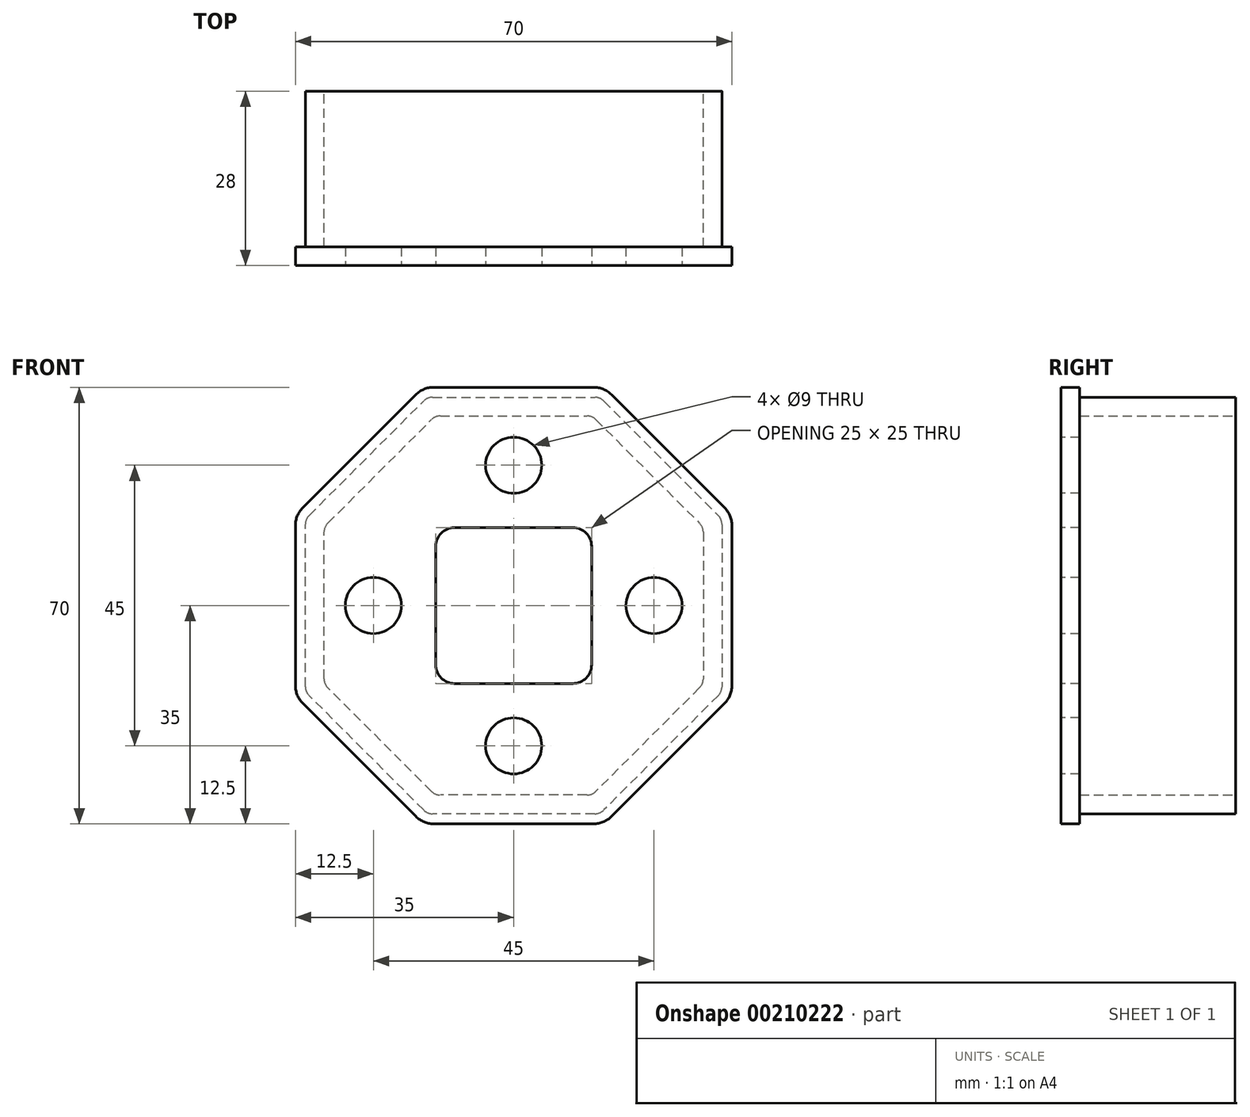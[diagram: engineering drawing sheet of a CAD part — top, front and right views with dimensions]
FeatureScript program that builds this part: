
annotation { "Feature Type Name" : "Feature", "Feature Type Description" : "" }
export const myFeature = defineFeature(function(context is Context, id is Id, definition is map)
    precondition{}
    {
        {
            var Q0;
            Q0=qCreatedBy(makeId("Front.planeOp"),FACE);
            var sketch = newSketch(context, id + "F0", { "sketchPlane" : qUnion([Q0])});
            skCircle(sketch, "E0.cCircle", {"center": v(0, 0) * mm, "radius": 33.4 * mm, "construction": true});
            skLineSegment(sketch, "E0.0", {"start": v(-13.83, 33.4) * mm, "end": v(13.83, 33.4) * mm});
            skLineSegment(sketch, "E0.1", {"start": v(13.83, 33.4) * mm, "end": v(33.4, 13.83) * mm});
            skLineSegment(sketch, "E0.2", {"start": v(33.4, 13.83) * mm, "end": v(33.4, -13.83) * mm});
            skLineSegment(sketch, "E0.3", {"start": v(33.4, -13.83) * mm, "end": v(13.83, -33.4) * mm});
            skLineSegment(sketch, "E0.4", {"start": v(13.83, -33.4) * mm, "end": v(-13.83, -33.4) * mm});
            skLineSegment(sketch, "E0.5", {"start": v(-13.83, -33.4) * mm, "end": v(-33.4, -13.83) * mm});
            skLineSegment(sketch, "E0.6", {"start": v(-33.4, -13.83) * mm, "end": v(-33.4, 13.83) * mm});
            skLineSegment(sketch, "E0.7", {"start": v(-33.4, 13.83) * mm, "end": v(-13.83, 33.4) * mm});
            skPoint(sketch, "E0.0.midPoint", {"position": v(0, 33.4) * mm});
            skLineSegment(sketch, "E1.0", {"start": v(-30.4, -12.6) * mm, "end": v(-30.4, 12.6) * mm});
            skLineSegment(sketch, "E1.1", {"start": v(-12.6, -30.4) * mm, "end": v(-30.4, -12.6) * mm});
            skLineSegment(sketch, "E1.2", {"start": v(-30.4, 12.6) * mm, "end": v(-12.6, 30.4) * mm});
            skLineSegment(sketch, "E1.3", {"start": v(12.6, -30.4) * mm, "end": v(-12.6, -30.4) * mm});
            skLineSegment(sketch, "E1.4", {"start": v(-12.6, 30.4) * mm, "end": v(12.6, 30.4) * mm});
            skLineSegment(sketch, "E1.5", {"start": v(12.6, 30.4) * mm, "end": v(30.4, 12.6) * mm});
            skLineSegment(sketch, "E1.6", {"start": v(30.4, 12.6) * mm, "end": v(30.4, -12.6) * mm});
            skLineSegment(sketch, "E1.7", {"start": v(30.4, -12.6) * mm, "end": v(12.6, -30.4) * mm});
            skSolve(sketch);
        }
        {
            var Q0;
            Q0=makeQuery(id+"F0.imprint","IMPRINT",FACE,{"disambiguationData":[TD([[makeQuery(id+"F0.imprint","IMPRINT",EDGE,{"derivedFrom":sQuery(id+"F0.wireOp",EDGE,"E0.0")}),-1.0]])]});
            extrude(context, id + "F1", {"entities" : qUnion([Q0]), "depth" : 25 * mm});
        }
        {
            var Q0;
            Q0=makeQuery(id+"F1.opExtrude","CAP_FACE",FACE,{"disambiguationData":[OSD([sQuery(id+"F0.wireOp",EDGE,"E0.0"),sQuery(id+"F0.wireOp",EDGE,"E0.1"),sQuery(id+"F0.wireOp",EDGE,"E0.2"),sQuery(id+"F0.wireOp",EDGE,"E0.3"),sQuery(id+"F0.wireOp",EDGE,"E0.4"),sQuery(id+"F0.wireOp",EDGE,"E0.5"),sQuery(id+"F0.wireOp",EDGE,"E0.6"),sQuery(id+"F0.wireOp",EDGE,"E0.7"),sQuery(id+"F0.wireOp",EDGE,"E1.0"),sQuery(id+"F0.wireOp",EDGE,"E1.1"),sQuery(id+"F0.wireOp",EDGE,"E1.2"),sQuery(id+"F0.wireOp",EDGE,"E1.3"),sQuery(id+"F0.wireOp",EDGE,"E1.4"),sQuery(id+"F0.wireOp",EDGE,"E1.5"),sQuery(id+"F0.wireOp",EDGE,"E1.6"),sQuery(id+"F0.wireOp",EDGE,"E1.7")])],"isStart":false});
            var sketch = newSketch(context, id + "F2", { "sketchPlane" : qUnion([Q0])});
            skCircle(sketch, "E2.cCircle", {"center": v(0, 0) * mm, "radius": 35 * mm, "construction": true});
            skLineSegment(sketch, "E2.0", {"start": v(-14.5, 35) * mm, "end": v(14.5, 35) * mm});
            skLineSegment(sketch, "E2.1", {"start": v(14.5, 35) * mm, "end": v(35, 14.5) * mm});
            skLineSegment(sketch, "E2.2", {"start": v(35, 14.5) * mm, "end": v(35, -14.5) * mm});
            skLineSegment(sketch, "E2.3", {"start": v(35, -14.5) * mm, "end": v(14.5, -35) * mm});
            skLineSegment(sketch, "E2.4", {"start": v(14.5, -35) * mm, "end": v(-14.5, -35) * mm});
            skLineSegment(sketch, "E2.5", {"start": v(-14.5, -35) * mm, "end": v(-35, -14.5) * mm});
            skLineSegment(sketch, "E2.6", {"start": v(-35, -14.5) * mm, "end": v(-35, 14.5) * mm});
            skLineSegment(sketch, "E2.7", {"start": v(-35, 14.5) * mm, "end": v(-14.5, 35) * mm});
            skPoint(sketch, "E2.0.midPoint", {"position": v(0, 35) * mm});
            skSolve(sketch);
        }
        {
            var Q0;
            Q0 = qSketchRegion(id + "F2", true);
            extrude(context, id + "F3", {"entities" : qUnion([Q0]), "operationType" : NewBodyOperationType.ADD, "depth" : 3 * mm});
        }
        {
            var Q0;
            Q0=makeQuery(id+"F1.opExtrude","SWEPT_EDGE",EDGE,{"disambiguationData":[OSD([sQuery(id+"F0.wireOp",EDGE,"E0.0"),sQuery(id+"F0.wireOp",EDGE,"E0.1")])]});
            var Q1;
            Q1=makeQuery(id+"F1.opExtrude","SWEPT_EDGE",EDGE,{"disambiguationData":[OSD([sQuery(id+"F0.wireOp",EDGE,"E0.1"),sQuery(id+"F0.wireOp",EDGE,"E0.2")])]});
            var Q2;
            Q2=makeQuery(id+"F1.opExtrude","SWEPT_EDGE",EDGE,{"disambiguationData":[OSD([sQuery(id+"F0.wireOp",EDGE,"E0.2"),sQuery(id+"F0.wireOp",EDGE,"E0.3")])]});
            var Q3;
            Q3=makeQuery(id+"F1.opExtrude","SWEPT_EDGE",EDGE,{"disambiguationData":[OSD([sQuery(id+"F0.wireOp",EDGE,"E0.3"),sQuery(id+"F0.wireOp",EDGE,"E0.4")])]});
            var Q4;
            Q4=makeQuery(id+"F1.opExtrude","SWEPT_EDGE",EDGE,{"disambiguationData":[OSD([sQuery(id+"F0.wireOp",EDGE,"E0.4"),sQuery(id+"F0.wireOp",EDGE,"E0.5")])]});
            var Q5;
            Q5=makeQuery(id+"F1.opExtrude","SWEPT_EDGE",EDGE,{"disambiguationData":[OSD([sQuery(id+"F0.wireOp",EDGE,"E0.5"),sQuery(id+"F0.wireOp",EDGE,"E0.6")])]});
            var Q6;
            Q6=makeQuery(id+"F1.opExtrude","SWEPT_EDGE",EDGE,{"disambiguationData":[OSD([sQuery(id+"F0.wireOp",EDGE,"E0.6"),sQuery(id+"F0.wireOp",EDGE,"E0.7")])]});
            var Q7;
            Q7=makeQuery(id+"F1.opExtrude","SWEPT_EDGE",EDGE,{"disambiguationData":[OSD([sQuery(id+"F0.wireOp",EDGE,"E0.0"),sQuery(id+"F0.wireOp",EDGE,"E0.7")])]});
            var Q8;
            Q8=makeQuery(id+"F1.opExtrude","SWEPT_EDGE",EDGE,{"disambiguationData":[OSD([sQuery(id+"F0.wireOp",EDGE,"E1.0"),sQuery(id+"F0.wireOp",EDGE,"E1.2")])]});
            var Q9;
            Q9=makeQuery(id+"F1.opExtrude","SWEPT_EDGE",EDGE,{"disambiguationData":[OSD([sQuery(id+"F0.wireOp",EDGE,"E1.0"),sQuery(id+"F0.wireOp",EDGE,"E1.1")])]});
            var Q10;
            Q10=makeQuery(id+"F1.opExtrude","SWEPT_EDGE",EDGE,{"disambiguationData":[OSD([sQuery(id+"F0.wireOp",EDGE,"E1.2"),sQuery(id+"F0.wireOp",EDGE,"E1.4")])]});
            var Q11;
            Q11=makeQuery(id+"F1.opExtrude","SWEPT_EDGE",EDGE,{"disambiguationData":[OSD([sQuery(id+"F0.wireOp",EDGE,"E1.4"),sQuery(id+"F0.wireOp",EDGE,"E1.5")])]});
            var Q12;
            Q12=makeQuery(id+"F1.opExtrude","SWEPT_EDGE",EDGE,{"disambiguationData":[OSD([sQuery(id+"F0.wireOp",EDGE,"E1.5"),sQuery(id+"F0.wireOp",EDGE,"E1.6")])]});
            var Q13;
            Q13=makeQuery(id+"F1.opExtrude","SWEPT_EDGE",EDGE,{"disambiguationData":[OSD([sQuery(id+"F0.wireOp",EDGE,"E1.6"),sQuery(id+"F0.wireOp",EDGE,"E1.7")])]});
            var Q14;
            Q14=makeQuery(id+"F1.opExtrude","SWEPT_EDGE",EDGE,{"disambiguationData":[OSD([sQuery(id+"F0.wireOp",EDGE,"E1.1"),sQuery(id+"F0.wireOp",EDGE,"E1.3")])]});
            var Q15;
            Q15=makeQuery(id+"F1.opExtrude","SWEPT_EDGE",EDGE,{"disambiguationData":[OSD([sQuery(id+"F0.wireOp",EDGE,"E1.3"),sQuery(id+"F0.wireOp",EDGE,"E1.7")])]});
            fillet(context, id + "F4", {"entities" : qUnion([Q0, Q1, Q2, Q3, Q4, Q5, Q6, Q7, Q8, Q9, Q10, Q11, Q12, Q13, Q14, Q15]), "radius" : 2 * mm, "tangentPropagation" : true, "allowEdgeOverflow" : false});
        }
        {
            var Q0;
            Q0=makeQuery(id+"F3.opExtrude","SWEPT_EDGE",EDGE,{"disambiguationData":[OSD([sQuery(id+"F2.wireOp",EDGE,"E2.0"),sQuery(id+"F2.wireOp",EDGE,"E2.7")])]});
            var Q1;
            Q1=makeQuery(id+"F3.opExtrude","SWEPT_EDGE",EDGE,{"disambiguationData":[OSD([sQuery(id+"F2.wireOp",EDGE,"E2.6"),sQuery(id+"F2.wireOp",EDGE,"E2.7")])]});
            var Q2;
            Q2=makeQuery(id+"F3.opExtrude","SWEPT_EDGE",EDGE,{"disambiguationData":[OSD([sQuery(id+"F2.wireOp",EDGE,"E2.0"),sQuery(id+"F2.wireOp",EDGE,"E2.1")])]});
            var Q3;
            Q3=makeQuery(id+"F3.opExtrude","SWEPT_EDGE",EDGE,{"disambiguationData":[OSD([sQuery(id+"F2.wireOp",EDGE,"E2.1"),sQuery(id+"F2.wireOp",EDGE,"E2.2")])]});
            var Q4;
            Q4=makeQuery(id+"F3.opExtrude","SWEPT_EDGE",EDGE,{"disambiguationData":[OSD([sQuery(id+"F2.wireOp",EDGE,"E2.2"),sQuery(id+"F2.wireOp",EDGE,"E2.3")])]});
            var Q5;
            Q5=makeQuery(id+"F3.opExtrude","SWEPT_EDGE",EDGE,{"disambiguationData":[OSD([sQuery(id+"F2.wireOp",EDGE,"E2.3"),sQuery(id+"F2.wireOp",EDGE,"E2.4")])]});
            var Q6;
            Q6=makeQuery(id+"F3.opExtrude","SWEPT_EDGE",EDGE,{"disambiguationData":[OSD([sQuery(id+"F2.wireOp",EDGE,"E2.4"),sQuery(id+"F2.wireOp",EDGE,"E2.5")])]});
            var Q7;
            Q7=makeQuery(id+"F3.opExtrude","SWEPT_EDGE",EDGE,{"disambiguationData":[OSD([sQuery(id+"F2.wireOp",EDGE,"E2.5"),sQuery(id+"F2.wireOp",EDGE,"E2.6")])]});
            fillet(context, id + "F5", {"entities" : qUnion([Q0, Q1, Q2, Q3, Q4, Q5, Q6, Q7]), "radius" : 4 * mm, "tangentPropagation" : true, "allowEdgeOverflow" : false});
        }
        {
            var Q0;
            Q0=makeQuery(id+"F3.opExtrude","CAP_FACE",FACE,{"disambiguationData":[OSD([sQuery(id+"F2.wireOp",EDGE,"E2.0"),sQuery(id+"F2.wireOp",EDGE,"E2.1"),sQuery(id+"F2.wireOp",EDGE,"E2.2"),sQuery(id+"F2.wireOp",EDGE,"E2.3"),sQuery(id+"F2.wireOp",EDGE,"E2.4"),sQuery(id+"F2.wireOp",EDGE,"E2.5"),sQuery(id+"F2.wireOp",EDGE,"E2.6"),sQuery(id+"F2.wireOp",EDGE,"E2.7")])],"isStart":false});
            var sketch = newSketch(context, id + "F6", { "sketchPlane" : qUnion([Q0])});
            skLineSegment(sketch, "E3.bottom", {"start": v(12.5, 12.5) * mm, "end": v(-12.5, 12.5) * mm});
            skLineSegment(sketch, "E3.top", {"start": v(12.5, -12.5) * mm, "end": v(-12.5, -12.5) * mm});
            skLineSegment(sketch, "E3.left", {"start": v(12.5, 12.5) * mm, "end": v(12.5, -12.5) * mm});
            skLineSegment(sketch, "E3.right", {"start": v(-12.5, 12.5) * mm, "end": v(-12.5, -12.5) * mm});
            skPoint(sketch, "E3.middle", {"position": v(0, 0) * mm});
            skSolve(sketch);
        }
        {
            var Q0;
            Q0 = qSketchRegion(id + "F6", true);
            extrude(context, id + "F7", {"entities" : qUnion([Q0]), "operationType" : NewBodyOperationType.REMOVE, "oppositeDirection" : true, "depth" : 25 * mm});
        }
        {
            var Q0;
            Q0=makeQuery(id+"F7.boolean.opBoolean","COPY",EDGE,{"derivedFrom":makeQuery(id+"F7.opExtrude","SWEPT_EDGE",EDGE,{"disambiguationData":[OSD([sQuery(id+"F6.wireOp",EDGE,"E3.bottom"),sQuery(id+"F6.wireOp",EDGE,"E3.right")])]})});
            var Q1;
            Q1=makeQuery(id+"F7.boolean.opBoolean","COPY",EDGE,{"derivedFrom":makeQuery(id+"F7.opExtrude","SWEPT_EDGE",EDGE,{"disambiguationData":[OSD([sQuery(id+"F6.wireOp",EDGE,"E3.bottom"),sQuery(id+"F6.wireOp",EDGE,"E3.left")])]})});
            var Q2;
            Q2=makeQuery(id+"F7.boolean.opBoolean","COPY",EDGE,{"derivedFrom":makeQuery(id+"F7.opExtrude","SWEPT_EDGE",EDGE,{"disambiguationData":[OSD([sQuery(id+"F6.wireOp",EDGE,"E3.top"),sQuery(id+"F6.wireOp",EDGE,"E3.left")])]})});
            var Q3;
            Q3=makeQuery(id+"F7.boolean.opBoolean","COPY",EDGE,{"derivedFrom":makeQuery(id+"F7.opExtrude","SWEPT_EDGE",EDGE,{"disambiguationData":[OSD([sQuery(id+"F6.wireOp",EDGE,"E3.top"),sQuery(id+"F6.wireOp",EDGE,"E3.right")])]})});
            fillet(context, id + "F8", {"entities" : qUnion([Q0, Q1, Q2, Q3]), "radius" : 3 * mm, "tangentPropagation" : true, "allowEdgeOverflow" : false});
        }
        {
            var Q0;
            Q0=makeQuery(id+"F3.opExtrude","CAP_FACE",FACE,{"disambiguationData":[OSD([sQuery(id+"F2.wireOp",EDGE,"E2.0"),sQuery(id+"F2.wireOp",EDGE,"E2.1"),sQuery(id+"F2.wireOp",EDGE,"E2.2"),sQuery(id+"F2.wireOp",EDGE,"E2.3"),sQuery(id+"F2.wireOp",EDGE,"E2.4"),sQuery(id+"F2.wireOp",EDGE,"E2.5"),sQuery(id+"F2.wireOp",EDGE,"E2.6"),sQuery(id+"F2.wireOp",EDGE,"E2.7")])],"isStart":false});
            var sketch = newSketch(context, id + "F9", { "sketchPlane" : qUnion([Q0])});
            skCircle(sketch, "E4", {"center": v(0, 0) * mm, "radius": 22.5 * mm, "construction": true});
            skLineSegment(sketch, "E5", {"start": v(0, 22.5) * mm, "end": v(0, -22.5) * mm, "construction": true});
            skPoint(sketch, "E5.endSnap0", {"position": v(0, -12.5) * mm});
            skLineSegment(sketch, "E6", {"start": v(-22.5, 0) * mm, "end": v(22.5, 0) * mm, "construction": true});
            skCircle(sketch, "E7", {"center": v(0, 22.5) * mm, "radius": 4.5 * mm});
            skCircle(sketch, "E8", {"center": v(22.5, 0) * mm, "radius": 4.5 * mm});
            skCircle(sketch, "E9", {"center": v(0, -22.5) * mm, "radius": 4.5 * mm});
            skCircle(sketch, "E10", {"center": v(-22.5, 0) * mm, "radius": 4.5 * mm});
            skSolve(sketch);
        }
        {
            var Q0;
            Q0 = qSketchRegion(id + "F9", true);
            extrude(context, id + "F10", {"entities" : qUnion([Q0]), "operationType" : NewBodyOperationType.REMOVE, "oppositeDirection" : true, "depth" : 25 * mm});
        }
    });
